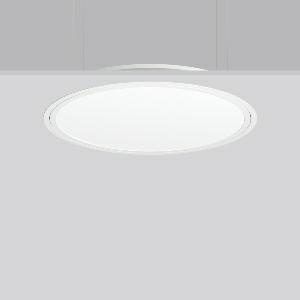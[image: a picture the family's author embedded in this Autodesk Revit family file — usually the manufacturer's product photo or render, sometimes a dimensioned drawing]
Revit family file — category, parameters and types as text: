
# Revit family: triona_round_e_312383_002_12_7031
name_source: partatom
category: Lighting Fixtures
units: mm (PartAtom-declared; Revit-internal decimal feet)

## family parameters
Cut with Voids When Loaded = No
Host = Face
Light Source = No
Part Type = Normal
Room Calculation Point = No
Round Connector Dimension = Use Diameter
Shared = No

## types (1)
- TRIONA round E (1 x LED Modul 830, 6450 lm, 3000)
    Apparent Load = 70 VA
    CIE Flux Codes = 49 80 96 100 100
    Color Rendering = 80
    Color Temperature = 3000
    Default Elevation = 1800 mm
    Description = Series: TRIONA round
Decorative round LED recessed surface luminaire. Cover made of sheet steel, powder-coated. Frame made of aluminium, powder-coated. Recessed ring: aluminium extrusion profile, powder coated. Light emission through a diffuser: plastic, opal. Lightguide and diffuser made of non-yellowing plastic (PMMA). Lateral light emission (RZB SIDELITE technology) for above-average homogeneous light distribution. Suitable for installation in cavity ceilings. Tool-free mounting system thanks to the rocker arm mechanism (patent pending). Electronic ballast included. Very easy installation thanks to Plug+Play connection. 
Colour: traffic white, matt (RAL 9016)
Diameter: 725 mm
Height: 2 mm
Cut-out diameter: 702 mm
Recess height: 100 mm
Luminaire: recess height: 89 mm
Lamp: LED
Socket: without socket
Colour temperature: 3000K
Colour rendering index (CRI): 80
System power: 70 W
Rated luminous flux: 6450 lm
Luminous efficiency: 92 lm/W
Control gear: Converter, dimmable, DALI
Protection class: I
Type of protection: IP 40
    Height = 0 mm  [stored 0 ft]
    Lamp = 1 x LED Modul 830
    Lamp Light Flux = 6450 lm
    Lamp count = 1
    Length = 725 mm
    Lifetime = 50000 h
    Luminous efficacy = 92 lm/W
    Manufacturer = RZB
    ModVariant = No
    Model = 312383.002.12
    Mounting Place = Ceiling
    Mounting Type = Recessed
    Number of Poles = 1
    OnlyDefault = Yes
    Power Factor = 1
    Product Name = TRIONA round E
    Product group = Recessed modular luminaires
    ProductGroupID = 406
    Protection Class = Protection class I
    Protection Degree = IP 20
    RLX_Detail_Level = 1
    RLX_Emergency_Light_Flux = 0 lm
    RLX_Emergency_Type = 0
    RLX_Emergency_Type_DB = No
    RlxData = <blob elided: 34833 chars, md5=6999f0c1>
    Socket = socket
    Standby Power = 0 W
    System Light Flux = 6450 lm
    System Power = 70 W
    Type Comments = Product without accessories
    Type Image = 312383.002.12.jpg
    URL = http://relux.com
    VarID = ---
    Voltage = 230 V
    Voltage Range = 220-240 V
    Weight = 0.00 kg
    Width = 0 mm  [stored 0 ft]

note: [stored X ft] marks values corroborated as IEEE doubles in the binary element streams (Revit-internal decimal feet)

## geometry (parser evidence)
native form markers: Blend x4, Sweep x11
no freeform markers — native parametric forms only
